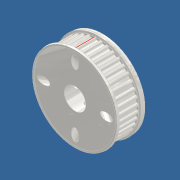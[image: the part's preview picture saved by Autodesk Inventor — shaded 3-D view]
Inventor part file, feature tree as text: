
AUTODESK INVENTOR PART (.ipt)
format: ipt  version: 2020 (Build 240168000, 168)  size: 688,640 bytes
history: native  units: mm (DEFAULTED — no unit token found)
features: other x6, extrude x4, sketch x4, pattern_circular x2, hole x2, fillet x1, plane x1, reference x1, projected_geometry x1
ambient origin geometry x8: Origin, YZ Plane, XZ Plane, XY Plane, X Axis, Y Axis, Z Axis, Center Point
bodies: Solid1 (feature_tree)
feature tree (22):
  other  "Pulley Sketch"
  extrude  "Base Body"  Depth=0.3mm
  extrude  "Tooth"  Depth=8.726646mm
  fillet  "Tooth Fillet"  Radius=1.05mm
  pattern_circular  "Teeth"  [2 undecoded]
  other  "Left flange"
  other  "Right flange"
  hole  "Hole1"  [1 undecoded]
  extrude  "Extrusion3"  Depth=1.0mm
  plane  "Work Plane3"
  hole  "Hole2"  [1 undecoded]
  pattern_circular  "Circular Pattern2"  Count=40  [1 undecoded]
  extrude  "Extrusion5"  TaperAngle=360.0deg  [1 undecoded]
  sketch  "Sketch2"  dims[d0=31.830989mm d1=0.3mm]
  sketch  "Sketch3"  dims[d2=0.75mm d3=8.726646mm d4=1.05mm]
  reference  "Reference1"
  sketch  "Sketch9"  dims[d5=8.0mm]
  sketch  "Sketch10"  dims[d6=0.0mm d7=8.0mm d8=0.0mm d9=0.2mm d10=0.3mm d11=400.0mm d12=360.0deg d15=0.0mm d16=0.0mm d17=8.3mm d18=6.0mm d19=3.023mm d20=2.0mm d21=14.3117mm d22=8.0mm d23=0.0mm d24=11.0mm d25=2.0mm d26=0.0mm d32=3.0mm d33=2.8mm d34=6.0mm d35=3.023mm d36=2.0mm d37=14.3117mm d38=15.0mm d39=0.0mm d40=40.0mm d41=360.0deg d43=1.0mm d44=0.0mm]
  projected_geometry  "Projected Loop1"
  parser-record x1  (decoder bookkeeping rows leaked as tree rows — omitted from the tree; the rows remain in map.json)
  other  "10-03-00 AnsambluZ_V2.iam"
  other  "ISO 1224-1 (Metric) 18 - 8 x 16 x 4:1"
note: 6 required parameter values undecoded (feature->parameter linkage not recoverable at this tier; creation-order binding heuristic only, values carry confidence <= 0.55)
note: 1 file-system path scrubbed to <path> (originals preserved in map.json)
